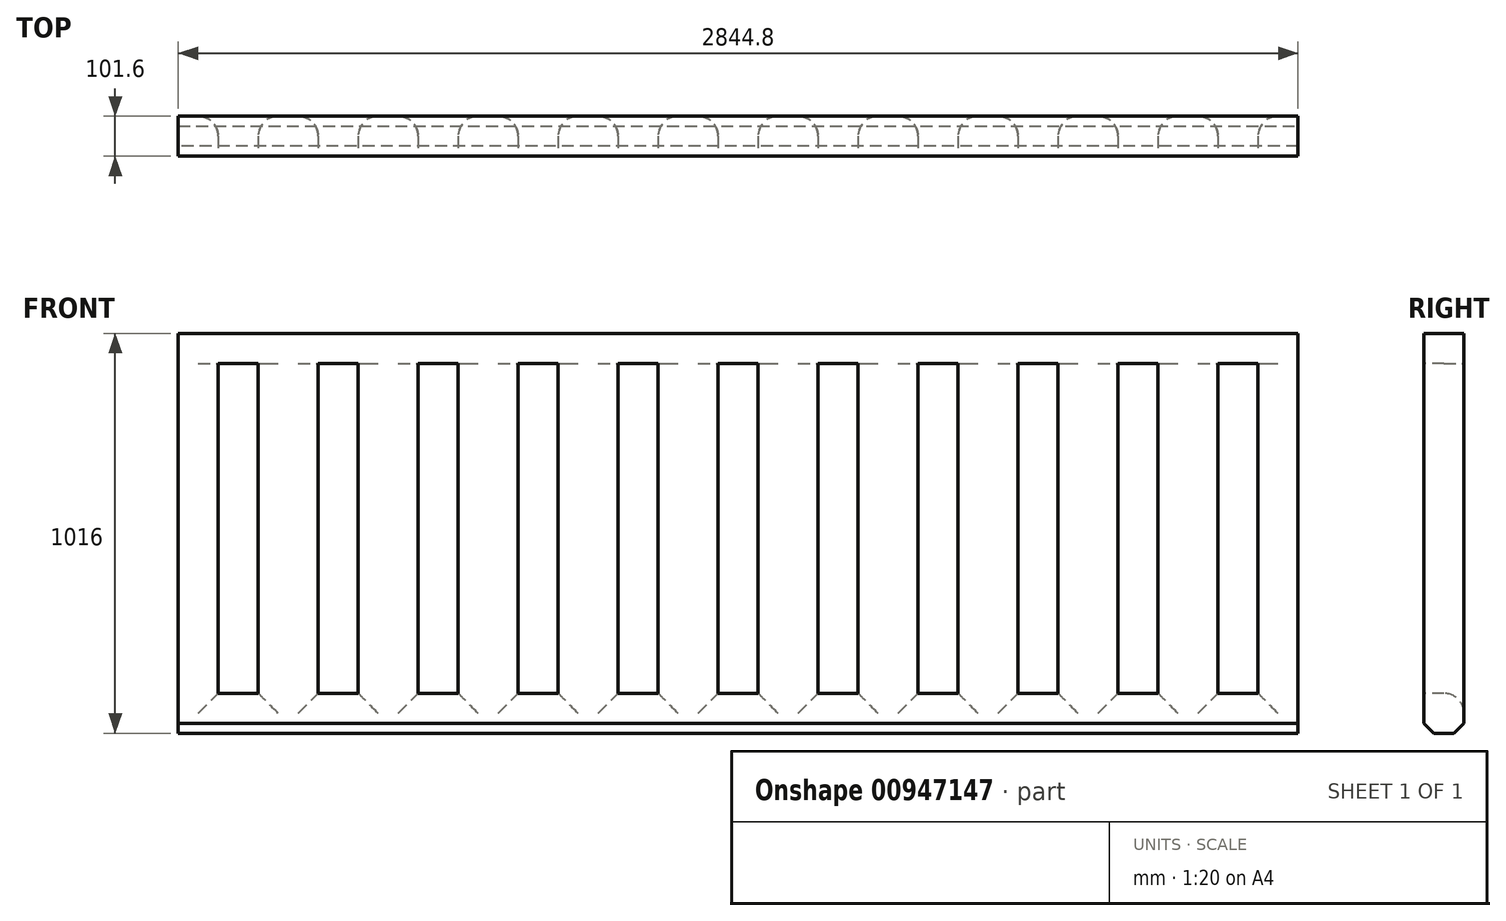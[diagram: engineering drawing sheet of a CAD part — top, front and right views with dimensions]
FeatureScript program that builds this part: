
annotation { "Feature Type Name" : "Feature", "Feature Type Description" : "" }
export const myFeature = defineFeature(function(context is Context, id is Id, definition is map)
    precondition{}
    {
        {
            var Q0;
            Q0=qCreatedBy(makeId("Front.planeOp"),FACE);
            var sketch = newSketch(context, id + "F0", { "sketchPlane" : qUnion([Q0])});
            skLineSegment(sketch, "E0.bottom", {"start": v(0, 0) * mm, "end": v(4368.8, 0) * mm});
            skLineSegment(sketch, "E0.top", {"start": v(0, 1016) * mm, "end": v(4368.8, 1016) * mm});
            skLineSegment(sketch, "E0.left", {"start": v(0, 0) * mm, "end": v(0, 1016) * mm});
            skLineSegment(sketch, "E0.right", {"start": v(4368.8, 0) * mm, "end": v(4368.8, 1016) * mm});
            skLineSegment(sketch, "E1", {"start": v(2844.8, 1016) * mm, "end": v(2844.8, 0) * mm});
            skSolve(sketch);
        }
        {
            var Q0;
            {var subQ0=sQuery(id+"F0.wireOp",EDGE,"E0.left");Q0=makeQuery(id+"F0.imprint","IMPRINT",FACE,{"disambiguationData":[TD([[makeQuery(id+"F0.imprint","IMPRINT",EDGE,{"derivedFrom":subQ0}),-1.0]])]});}
            extrude(context, id + "F1", {"entities" : qUnion([Q0]), "depth" : 101.6 * mm, "offsetDistance" : 25.4 * mm});
        }
        {
            var Q0;
            Q0=makeQuery(id+"F1.opExtrude","CAP_FACE",FACE,{"disambiguationData":[OSD([sQuery(id+"F0.wireOp",EDGE,"E0.bottom"),sQuery(id+"F0.wireOp",EDGE,"E0.top"),sQuery(id+"F0.wireOp",EDGE,"E0.left"),sQuery(id+"F0.wireOp",EDGE,"E0.right")])],"isStart":false});
            var sketch = newSketch(context, id + "F2", { "sketchPlane" : qUnion([Q0])});
            skLineSegment(sketch, "E2.left", {"start": v(101.6, 939.8) * mm, "end": v(101.6, 101.6) * mm});
            skLineSegment(sketch, "E2.right", {"start": v(203.2, 939.8) * mm, "end": v(203.2, 101.6) * mm});
            skLineSegment(sketch, "E3", {"start": v(101.6, 939.8) * mm, "end": v(203.2, 939.8) * mm});
            skLineSegment(sketch, "E4", {"start": v(101.6, 101.6) * mm, "end": v(203.2, 101.6) * mm});
            skLineSegment(sketch, "E5", {"start": v(0, 939.8) * mm, "end": v(2974.6, 939.8) * mm, "construction": true});
            skPoint(sketch, "E5.startSnap0", {"position": v(152.4, 939.8) * mm});
            skLineSegment(sketch, "E6", {"start": v(0, 101.6) * mm, "end": v(2947.62, 101.6) * mm, "construction": true});
            skLineSegment(sketch, "E7.bottom", {"start": v(355.6, 939.8) * mm, "end": v(457.2, 939.8) * mm});
            skLineSegment(sketch, "E7.top", {"start": v(355.6, 101.6) * mm, "end": v(457.2, 101.6) * mm});
            skLineSegment(sketch, "E7.left", {"start": v(355.6, 939.8) * mm, "end": v(355.6, 101.6) * mm});
            skLineSegment(sketch, "E7.right", {"start": v(457.2, 939.8) * mm, "end": v(457.2, 101.6) * mm});
            skLineSegment(sketch, "E8.bottom", {"start": v(609.6, 939.8) * mm, "end": v(711.2, 939.8) * mm});
            skLineSegment(sketch, "E8.top", {"start": v(609.6, 101.6) * mm, "end": v(711.2, 101.6) * mm});
            skLineSegment(sketch, "E8.left", {"start": v(609.6, 939.8) * mm, "end": v(609.6, 101.6) * mm});
            skLineSegment(sketch, "E8.right", {"start": v(711.2, 939.8) * mm, "end": v(711.2, 101.6) * mm});
            skLineSegment(sketch, "E9.bottom", {"start": v(863.6, 939.8) * mm, "end": v(965.2, 939.8) * mm});
            skLineSegment(sketch, "E9.top", {"start": v(863.6, 101.6) * mm, "end": v(965.2, 101.6) * mm});
            skLineSegment(sketch, "E9.left", {"start": v(863.6, 939.8) * mm, "end": v(863.6, 101.6) * mm});
            skLineSegment(sketch, "E9.right", {"start": v(965.2, 939.8) * mm, "end": v(965.2, 101.6) * mm});
            skLineSegment(sketch, "E10.bottom", {"start": v(1117.6, 939.8) * mm, "end": v(1219.2, 939.8) * mm});
            skLineSegment(sketch, "E10.top", {"start": v(1117.6, 101.6) * mm, "end": v(1219.2, 101.6) * mm});
            skLineSegment(sketch, "E10.left", {"start": v(1117.6, 939.8) * mm, "end": v(1117.6, 101.6) * mm});
            skLineSegment(sketch, "E10.right", {"start": v(1219.2, 939.8) * mm, "end": v(1219.2, 101.6) * mm});
            skLineSegment(sketch, "E11.bottom", {"start": v(1371.6, 939.8) * mm, "end": v(1473.2, 939.8) * mm});
            skLineSegment(sketch, "E11.top", {"start": v(1371.6, 101.6) * mm, "end": v(1473.2, 101.6) * mm});
            skLineSegment(sketch, "E11.left", {"start": v(1371.6, 939.8) * mm, "end": v(1371.6, 101.6) * mm});
            skLineSegment(sketch, "E11.right", {"start": v(1473.2, 939.8) * mm, "end": v(1473.2, 101.6) * mm});
            skLineSegment(sketch, "E12.bottom", {"start": v(1625.6, 939.8) * mm, "end": v(1727.2, 939.8) * mm});
            skLineSegment(sketch, "E12.top", {"start": v(1625.6, 101.6) * mm, "end": v(1727.2, 101.6) * mm});
            skLineSegment(sketch, "E12.left", {"start": v(1625.6, 939.8) * mm, "end": v(1625.6, 101.6) * mm});
            skLineSegment(sketch, "E12.right", {"start": v(1727.2, 939.8) * mm, "end": v(1727.2, 101.6) * mm});
            skLineSegment(sketch, "E13.bottom", {"start": v(1879.6, 939.8) * mm, "end": v(1981.2, 939.8) * mm});
            skLineSegment(sketch, "E13.top", {"start": v(1879.6, 101.6) * mm, "end": v(1981.2, 101.6) * mm});
            skLineSegment(sketch, "E13.left", {"start": v(1879.6, 939.8) * mm, "end": v(1879.6, 101.6) * mm});
            skLineSegment(sketch, "E13.right", {"start": v(1981.2, 939.8) * mm, "end": v(1981.2, 101.6) * mm});
            skLineSegment(sketch, "E14.bottom", {"start": v(2133.6, 939.8) * mm, "end": v(2235.2, 939.8) * mm});
            skLineSegment(sketch, "E14.top", {"start": v(2133.6, 101.6) * mm, "end": v(2235.2, 101.6) * mm});
            skLineSegment(sketch, "E14.left", {"start": v(2133.6, 939.8) * mm, "end": v(2133.6, 101.6) * mm});
            skLineSegment(sketch, "E14.right", {"start": v(2235.2, 939.8) * mm, "end": v(2235.2, 101.6) * mm});
            skLineSegment(sketch, "E15.bottom", {"start": v(2387.6, 939.8) * mm, "end": v(2489.2, 939.8) * mm});
            skLineSegment(sketch, "E15.top", {"start": v(2387.6, 101.6) * mm, "end": v(2489.2, 101.6) * mm});
            skLineSegment(sketch, "E15.left", {"start": v(2387.6, 939.8) * mm, "end": v(2387.6, 101.6) * mm});
            skLineSegment(sketch, "E15.right", {"start": v(2489.2, 939.8) * mm, "end": v(2489.2, 101.6) * mm});
            skLineSegment(sketch, "E16.bottom", {"start": v(2641.6, 939.8) * mm, "end": v(2743.2, 939.8) * mm});
            skLineSegment(sketch, "E16.top", {"start": v(2641.6, 101.6) * mm, "end": v(2743.2, 101.6) * mm});
            skLineSegment(sketch, "E16.left", {"start": v(2641.6, 939.8) * mm, "end": v(2641.6, 101.6) * mm});
            skLineSegment(sketch, "E16.right", {"start": v(2743.2, 939.8) * mm, "end": v(2743.2, 101.6) * mm});
            skLineSegment(sketch, "E17.bottom", {"start": v(2941.58, 939.8) * mm, "end": v(3043.18, 939.8) * mm});
            skLineSegment(sketch, "E17.top", {"start": v(2941.58, 101.6) * mm, "end": v(3043.18, 101.6) * mm});
            skLineSegment(sketch, "E17.left", {"start": v(2941.58, 939.8) * mm, "end": v(2941.58, 101.6) * mm});
            skLineSegment(sketch, "E17.right", {"start": v(3043.18, 939.8) * mm, "end": v(3043.18, 101.6) * mm});
            skSolve(sketch);
        }
        {
            var Q0;
            {var subQ0=sQuery(id+"F2.wireOp",EDGE,"E3");Q0=makeQuery(id+"F2.imprint","IMPRINT",FACE,{"disambiguationData":[TD([[makeQuery(id+"F2.imprint","IMPRINT",EDGE,{"derivedFrom":subQ0}),-1.0]])]});}
            var Q1;
            Q1=makeQuery(id+"F2.imprint","IMPRINT",FACE,{"disambiguationData":[TD([[makeQuery(id+"F2.imprint","IMPRINT",EDGE,{"derivedFrom":sQuery(id+"F2.wireOp",EDGE,"E7.bottom")}),-1.0]])]});
            var Q2;
            Q2=makeQuery(id+"F2.imprint","IMPRINT",FACE,{"disambiguationData":[TD([[makeQuery(id+"F2.imprint","IMPRINT",EDGE,{"derivedFrom":sQuery(id+"F2.wireOp",EDGE,"E8.bottom")}),-1.0]])]});
            var Q3;
            Q3=makeQuery(id+"F2.imprint","IMPRINT",FACE,{"disambiguationData":[TD([[makeQuery(id+"F2.imprint","IMPRINT",EDGE,{"derivedFrom":sQuery(id+"F2.wireOp",EDGE,"E9.bottom")}),-1.0]])]});
            var Q4;
            Q4=makeQuery(id+"F2.imprint","IMPRINT",FACE,{"disambiguationData":[TD([[makeQuery(id+"F2.imprint","IMPRINT",EDGE,{"derivedFrom":sQuery(id+"F2.wireOp",EDGE,"E10.bottom")}),-1.0]])]});
            var Q5;
            Q5=makeQuery(id+"F2.imprint","IMPRINT",FACE,{"disambiguationData":[TD([[makeQuery(id+"F2.imprint","IMPRINT",EDGE,{"derivedFrom":sQuery(id+"F2.wireOp",EDGE,"E11.bottom")}),-1.0]])]});
            var Q6;
            Q6=makeQuery(id+"F2.imprint","IMPRINT",FACE,{"disambiguationData":[TD([[makeQuery(id+"F2.imprint","IMPRINT",EDGE,{"derivedFrom":sQuery(id+"F2.wireOp",EDGE,"E12.bottom")}),-1.0]])]});
            var Q7;
            Q7=makeQuery(id+"F2.imprint","IMPRINT",FACE,{"disambiguationData":[TD([[makeQuery(id+"F2.imprint","IMPRINT",EDGE,{"derivedFrom":sQuery(id+"F2.wireOp",EDGE,"E13.bottom")}),-1.0]])]});
            var Q8;
            Q8=makeQuery(id+"F2.imprint","IMPRINT",FACE,{"disambiguationData":[TD([[makeQuery(id+"F2.imprint","IMPRINT",EDGE,{"derivedFrom":sQuery(id+"F2.wireOp",EDGE,"E14.bottom")}),-1.0]])]});
            var Q9;
            Q9=makeQuery(id+"F2.imprint","IMPRINT",FACE,{"disambiguationData":[TD([[makeQuery(id+"F2.imprint","IMPRINT",EDGE,{"derivedFrom":sQuery(id+"F2.wireOp",EDGE,"E15.bottom")}),-1.0]])]});
            var Q10;
            Q10=makeQuery(id+"F2.imprint","IMPRINT",FACE,{"disambiguationData":[TD([[makeQuery(id+"F2.imprint","IMPRINT",EDGE,{"derivedFrom":sQuery(id+"F2.wireOp",EDGE,"E16.bottom")}),-1.0]])]});
            extrude(context, id + "F3", {"entities" : qUnion([Q0, Q1, Q2, Q3, Q4, Q5, Q6, Q7, Q8, Q9, Q10]), "operationType" : NewBodyOperationType.REMOVE, "oppositeDirection" : true, "depth" : 307.34 * mm, "offsetDistance" : 25.4 * mm});
        }
        {
            var Q0;
            Q0=makeQuery(id+"F3.boolean.opBoolean","COPY",EDGE,{"derivedFrom":makeQuery(id+"F3.opExtrude","CAP_EDGE",EDGE,{"disambiguationData":[OSD([sQuery(id+"F2.wireOp",EDGE,"E2.left")])],"isStart":true})});
            var Q1;
            Q1=makeQuery(id+"F3.boolean.opBoolean","COPY",EDGE,{"derivedFrom":makeQuery(id+"F3.opExtrude","CAP_EDGE",EDGE,{"disambiguationData":[OSD([sQuery(id+"F2.wireOp",EDGE,"E3")])],"isStart":true})});
            var Q2;
            Q2=makeQuery(id+"F3.boolean.opBoolean","COPY",EDGE,{"derivedFrom":makeQuery(id+"F3.opExtrude","CAP_EDGE",EDGE,{"disambiguationData":[OSD([sQuery(id+"F2.wireOp",EDGE,"E2.right")])],"isStart":true})});
            var Q3;
            Q3=makeQuery(id+"F3.boolean.opBoolean","COPY",EDGE,{"derivedFrom":makeQuery(id+"F3.opExtrude","CAP_EDGE",EDGE,{"disambiguationData":[OSD([sQuery(id+"F2.wireOp",EDGE,"E4")])],"isStart":true})});
            var Q4;
            Q4=makeQuery(id+"F3.boolean.opBoolean","COPY",EDGE,{"derivedFrom":makeQuery(id+"F3.opExtrude","CAP_EDGE",EDGE,{"disambiguationData":[OSD([sQuery(id+"F2.wireOp",EDGE,"E7.left")])],"isStart":true})});
            var Q5;
            Q5=makeQuery(id+"F3.boolean.opBoolean","COPY",EDGE,{"derivedFrom":makeQuery(id+"F3.opExtrude","CAP_EDGE",EDGE,{"disambiguationData":[OSD([sQuery(id+"F2.wireOp",EDGE,"E7.bottom")])],"isStart":true})});
            var Q6;
            Q6=makeQuery(id+"F3.boolean.opBoolean","COPY",EDGE,{"derivedFrom":makeQuery(id+"F3.opExtrude","CAP_EDGE",EDGE,{"disambiguationData":[OSD([sQuery(id+"F2.wireOp",EDGE,"E7.right")])],"isStart":true})});
            var Q7;
            Q7=makeQuery(id+"F3.boolean.opBoolean","COPY",EDGE,{"derivedFrom":makeQuery(id+"F3.opExtrude","CAP_EDGE",EDGE,{"disambiguationData":[OSD([sQuery(id+"F2.wireOp",EDGE,"E7.top")])],"isStart":true})});
            var Q8;
            Q8=makeQuery(id+"F3.boolean.opBoolean","COPY",EDGE,{"derivedFrom":makeQuery(id+"F3.opExtrude","CAP_EDGE",EDGE,{"disambiguationData":[OSD([sQuery(id+"F2.wireOp",EDGE,"E8.left")])],"isStart":true})});
            var Q9;
            Q9=makeQuery(id+"F3.boolean.opBoolean","COPY",EDGE,{"derivedFrom":makeQuery(id+"F3.opExtrude","CAP_EDGE",EDGE,{"disambiguationData":[OSD([sQuery(id+"F2.wireOp",EDGE,"E8.top")])],"isStart":true})});
            var Q10;
            Q10=makeQuery(id+"F3.boolean.opBoolean","COPY",EDGE,{"derivedFrom":makeQuery(id+"F3.opExtrude","CAP_EDGE",EDGE,{"disambiguationData":[OSD([sQuery(id+"F2.wireOp",EDGE,"E8.right")])],"isStart":true})});
            var Q11;
            Q11=makeQuery(id+"F3.boolean.opBoolean","COPY",EDGE,{"derivedFrom":makeQuery(id+"F3.opExtrude","CAP_EDGE",EDGE,{"disambiguationData":[OSD([sQuery(id+"F2.wireOp",EDGE,"E8.bottom")])],"isStart":true})});
            var Q12;
            Q12=makeQuery(id+"F3.boolean.opBoolean","COPY",EDGE,{"derivedFrom":makeQuery(id+"F3.opExtrude","CAP_EDGE",EDGE,{"disambiguationData":[OSD([sQuery(id+"F2.wireOp",EDGE,"E9.left")])],"isStart":true})});
            var Q13;
            Q13=makeQuery(id+"F3.boolean.opBoolean","COPY",EDGE,{"derivedFrom":makeQuery(id+"F3.opExtrude","CAP_EDGE",EDGE,{"disambiguationData":[OSD([sQuery(id+"F2.wireOp",EDGE,"E9.bottom")])],"isStart":true})});
            var Q14;
            Q14=makeQuery(id+"F3.boolean.opBoolean","COPY",EDGE,{"derivedFrom":makeQuery(id+"F3.opExtrude","CAP_EDGE",EDGE,{"disambiguationData":[OSD([sQuery(id+"F2.wireOp",EDGE,"E9.right")])],"isStart":true})});
            var Q15;
            Q15=makeQuery(id+"F3.boolean.opBoolean","COPY",EDGE,{"derivedFrom":makeQuery(id+"F3.opExtrude","CAP_EDGE",EDGE,{"disambiguationData":[OSD([sQuery(id+"F2.wireOp",EDGE,"E9.top")])],"isStart":true})});
            var Q16;
            Q16=makeQuery(id+"F3.boolean.opBoolean","COPY",EDGE,{"derivedFrom":makeQuery(id+"F3.opExtrude","CAP_EDGE",EDGE,{"disambiguationData":[OSD([sQuery(id+"F2.wireOp",EDGE,"E10.left")])],"isStart":true})});
            var Q17;
            Q17=makeQuery(id+"F3.boolean.opBoolean","COPY",EDGE,{"derivedFrom":makeQuery(id+"F3.opExtrude","CAP_EDGE",EDGE,{"disambiguationData":[OSD([sQuery(id+"F2.wireOp",EDGE,"E10.top")])],"isStart":true})});
            var Q18;
            Q18=makeQuery(id+"F3.boolean.opBoolean","COPY",EDGE,{"derivedFrom":makeQuery(id+"F3.opExtrude","CAP_EDGE",EDGE,{"disambiguationData":[OSD([sQuery(id+"F2.wireOp",EDGE,"E10.right")])],"isStart":true})});
            var Q19;
            Q19=makeQuery(id+"F3.boolean.opBoolean","COPY",EDGE,{"derivedFrom":makeQuery(id+"F3.opExtrude","CAP_EDGE",EDGE,{"disambiguationData":[OSD([sQuery(id+"F2.wireOp",EDGE,"E10.bottom")])],"isStart":true})});
            var Q20;
            Q20=makeQuery(id+"F3.boolean.opBoolean","COPY",EDGE,{"derivedFrom":makeQuery(id+"F3.opExtrude","CAP_EDGE",EDGE,{"disambiguationData":[OSD([sQuery(id+"F2.wireOp",EDGE,"E11.bottom")])],"isStart":true})});
            var Q21;
            Q21=makeQuery(id+"F3.boolean.opBoolean","COPY",EDGE,{"derivedFrom":makeQuery(id+"F3.opExtrude","CAP_EDGE",EDGE,{"disambiguationData":[OSD([sQuery(id+"F2.wireOp",EDGE,"E11.left")])],"isStart":true})});
            var Q22;
            Q22=makeQuery(id+"F3.boolean.opBoolean","COPY",EDGE,{"derivedFrom":makeQuery(id+"F3.opExtrude","CAP_EDGE",EDGE,{"disambiguationData":[OSD([sQuery(id+"F2.wireOp",EDGE,"E11.right")])],"isStart":true})});
            var Q23;
            Q23=makeQuery(id+"F3.boolean.opBoolean","COPY",EDGE,{"derivedFrom":makeQuery(id+"F3.opExtrude","CAP_EDGE",EDGE,{"disambiguationData":[OSD([sQuery(id+"F2.wireOp",EDGE,"E11.top")])],"isStart":true})});
            var Q24;
            Q24=makeQuery(id+"F3.boolean.opBoolean","COPY",EDGE,{"derivedFrom":makeQuery(id+"F3.opExtrude","CAP_EDGE",EDGE,{"disambiguationData":[OSD([sQuery(id+"F2.wireOp",EDGE,"E12.top")])],"isStart":true})});
            var Q25;
            Q25=makeQuery(id+"F3.boolean.opBoolean","COPY",EDGE,{"derivedFrom":makeQuery(id+"F3.opExtrude","CAP_EDGE",EDGE,{"disambiguationData":[OSD([sQuery(id+"F2.wireOp",EDGE,"E12.left")])],"isStart":true})});
            var Q26;
            Q26=makeQuery(id+"F3.boolean.opBoolean","COPY",EDGE,{"derivedFrom":makeQuery(id+"F3.opExtrude","CAP_EDGE",EDGE,{"disambiguationData":[OSD([sQuery(id+"F2.wireOp",EDGE,"E12.right")])],"isStart":true})});
            var Q27;
            Q27=makeQuery(id+"F3.boolean.opBoolean","COPY",EDGE,{"derivedFrom":makeQuery(id+"F3.opExtrude","CAP_EDGE",EDGE,{"disambiguationData":[OSD([sQuery(id+"F2.wireOp",EDGE,"E12.bottom")])],"isStart":true})});
            var Q28;
            Q28=makeQuery(id+"F3.boolean.opBoolean","COPY",EDGE,{"derivedFrom":makeQuery(id+"F3.opExtrude","CAP_EDGE",EDGE,{"disambiguationData":[OSD([sQuery(id+"F2.wireOp",EDGE,"E13.left")])],"isStart":true})});
            var Q29;
            Q29=makeQuery(id+"F3.boolean.opBoolean","COPY",EDGE,{"derivedFrom":makeQuery(id+"F3.opExtrude","CAP_EDGE",EDGE,{"disambiguationData":[OSD([sQuery(id+"F2.wireOp",EDGE,"E13.bottom")])],"isStart":true})});
            var Q30;
            Q30=makeQuery(id+"F3.boolean.opBoolean","COPY",EDGE,{"derivedFrom":makeQuery(id+"F3.opExtrude","CAP_EDGE",EDGE,{"disambiguationData":[OSD([sQuery(id+"F2.wireOp",EDGE,"E13.right")])],"isStart":true})});
            var Q31;
            Q31=makeQuery(id+"F3.boolean.opBoolean","COPY",EDGE,{"derivedFrom":makeQuery(id+"F3.opExtrude","CAP_EDGE",EDGE,{"disambiguationData":[OSD([sQuery(id+"F2.wireOp",EDGE,"E13.top")])],"isStart":true})});
            var Q32;
            Q32=makeQuery(id+"F3.boolean.opBoolean","COPY",EDGE,{"derivedFrom":makeQuery(id+"F3.opExtrude","CAP_EDGE",EDGE,{"disambiguationData":[OSD([sQuery(id+"F2.wireOp",EDGE,"E14.top")])],"isStart":true})});
            var Q33;
            Q33=makeQuery(id+"F3.boolean.opBoolean","COPY",EDGE,{"derivedFrom":makeQuery(id+"F3.opExtrude","CAP_EDGE",EDGE,{"disambiguationData":[OSD([sQuery(id+"F2.wireOp",EDGE,"E14.left")])],"isStart":true})});
            var Q34;
            Q34=makeQuery(id+"F3.boolean.opBoolean","COPY",EDGE,{"derivedFrom":makeQuery(id+"F3.opExtrude","CAP_EDGE",EDGE,{"disambiguationData":[OSD([sQuery(id+"F2.wireOp",EDGE,"E14.right")])],"isStart":true})});
            var Q35;
            Q35=makeQuery(id+"F3.boolean.opBoolean","COPY",EDGE,{"derivedFrom":makeQuery(id+"F3.opExtrude","CAP_EDGE",EDGE,{"disambiguationData":[OSD([sQuery(id+"F2.wireOp",EDGE,"E14.bottom")])],"isStart":true})});
            var Q36;
            Q36=makeQuery(id+"F3.boolean.opBoolean","COPY",EDGE,{"derivedFrom":makeQuery(id+"F3.opExtrude","CAP_EDGE",EDGE,{"disambiguationData":[OSD([sQuery(id+"F2.wireOp",EDGE,"E15.bottom")])],"isStart":true})});
            var Q37;
            Q37=makeQuery(id+"F3.boolean.opBoolean","COPY",EDGE,{"derivedFrom":makeQuery(id+"F3.opExtrude","CAP_EDGE",EDGE,{"disambiguationData":[OSD([sQuery(id+"F2.wireOp",EDGE,"E15.left")])],"isStart":true})});
            var Q38;
            Q38=makeQuery(id+"F3.boolean.opBoolean","COPY",EDGE,{"derivedFrom":makeQuery(id+"F3.opExtrude","CAP_EDGE",EDGE,{"disambiguationData":[OSD([sQuery(id+"F2.wireOp",EDGE,"E15.right")])],"isStart":true})});
            var Q39;
            Q39=makeQuery(id+"F3.boolean.opBoolean","COPY",EDGE,{"derivedFrom":makeQuery(id+"F3.opExtrude","CAP_EDGE",EDGE,{"disambiguationData":[OSD([sQuery(id+"F2.wireOp",EDGE,"E15.top")])],"isStart":true})});
            var Q40;
            Q40=makeQuery(id+"F3.boolean.opBoolean","COPY",EDGE,{"derivedFrom":makeQuery(id+"F3.opExtrude","CAP_EDGE",EDGE,{"disambiguationData":[OSD([sQuery(id+"F2.wireOp",EDGE,"E16.left")])],"isStart":true})});
            var Q41;
            Q41=makeQuery(id+"F3.boolean.opBoolean","COPY",EDGE,{"derivedFrom":makeQuery(id+"F3.opExtrude","CAP_EDGE",EDGE,{"disambiguationData":[OSD([sQuery(id+"F2.wireOp",EDGE,"E16.top")])],"isStart":true})});
            var Q42;
            Q42=makeQuery(id+"F3.boolean.opBoolean","COPY",EDGE,{"derivedFrom":makeQuery(id+"F3.opExtrude","CAP_EDGE",EDGE,{"disambiguationData":[OSD([sQuery(id+"F2.wireOp",EDGE,"E16.right")])],"isStart":true})});
            var Q43;
            Q43=makeQuery(id+"F3.boolean.opBoolean","INTERSECT",EDGE,{"derivedFrom":[makeQuery(id+"F1.opExtrude","CAP_FACE",FACE,{"disambiguationData":[OSD([sQuery(id+"F0.wireOp",EDGE,"E0.bottom"),sQuery(id+"F0.wireOp",EDGE,"E0.top"),sQuery(id+"F0.wireOp",EDGE,"E0.left"),sQuery(id+"F0.wireOp",EDGE,"E1")])],"isStart":true}),makeQuery(id+"F3.opExtrude","SWEPT_FACE",FACE,{"disambiguationData":[OSD([sQuery(id+"F2.wireOp",EDGE,"E4")])]})]});
            var Q44;
            Q44=makeQuery(id+"F3.boolean.opBoolean","INTERSECT",EDGE,{"derivedFrom":[makeQuery(id+"F1.opExtrude","CAP_FACE",FACE,{"disambiguationData":[OSD([sQuery(id+"F0.wireOp",EDGE,"E0.bottom"),sQuery(id+"F0.wireOp",EDGE,"E0.top"),sQuery(id+"F0.wireOp",EDGE,"E0.left"),sQuery(id+"F0.wireOp",EDGE,"E1")])],"isStart":true}),makeQuery(id+"F3.opExtrude","SWEPT_FACE",FACE,{"disambiguationData":[OSD([sQuery(id+"F2.wireOp",EDGE,"E2.left")])]})]});
            var Q45;
            Q45=makeQuery(id+"F3.boolean.opBoolean","INTERSECT",EDGE,{"derivedFrom":[makeQuery(id+"F1.opExtrude","CAP_FACE",FACE,{"disambiguationData":[OSD([sQuery(id+"F0.wireOp",EDGE,"E0.bottom"),sQuery(id+"F0.wireOp",EDGE,"E0.top"),sQuery(id+"F0.wireOp",EDGE,"E0.left"),sQuery(id+"F0.wireOp",EDGE,"E1")])],"isStart":true}),makeQuery(id+"F3.opExtrude","SWEPT_FACE",FACE,{"disambiguationData":[OSD([sQuery(id+"F2.wireOp",EDGE,"E2.right")])]})]});
            var Q46;
            Q46=makeQuery(id+"F3.boolean.opBoolean","INTERSECT",EDGE,{"derivedFrom":[makeQuery(id+"F1.opExtrude","CAP_FACE",FACE,{"disambiguationData":[OSD([sQuery(id+"F0.wireOp",EDGE,"E0.bottom"),sQuery(id+"F0.wireOp",EDGE,"E0.top"),sQuery(id+"F0.wireOp",EDGE,"E0.left"),sQuery(id+"F0.wireOp",EDGE,"E1")])],"isStart":true}),makeQuery(id+"F3.opExtrude","SWEPT_FACE",FACE,{"disambiguationData":[OSD([sQuery(id+"F2.wireOp",EDGE,"E7.left")])]})]});
            var Q47;
            Q47=makeQuery(id+"F3.boolean.opBoolean","INTERSECT",EDGE,{"derivedFrom":[makeQuery(id+"F1.opExtrude","CAP_FACE",FACE,{"disambiguationData":[OSD([sQuery(id+"F0.wireOp",EDGE,"E0.bottom"),sQuery(id+"F0.wireOp",EDGE,"E0.top"),sQuery(id+"F0.wireOp",EDGE,"E0.left"),sQuery(id+"F0.wireOp",EDGE,"E1")])],"isStart":true}),makeQuery(id+"F3.opExtrude","SWEPT_FACE",FACE,{"disambiguationData":[OSD([sQuery(id+"F2.wireOp",EDGE,"E7.top")])]})]});
            var Q48;
            Q48=makeQuery(id+"F3.boolean.opBoolean","INTERSECT",EDGE,{"derivedFrom":[makeQuery(id+"F1.opExtrude","CAP_FACE",FACE,{"disambiguationData":[OSD([sQuery(id+"F0.wireOp",EDGE,"E0.bottom"),sQuery(id+"F0.wireOp",EDGE,"E0.top"),sQuery(id+"F0.wireOp",EDGE,"E0.left"),sQuery(id+"F0.wireOp",EDGE,"E1")])],"isStart":true}),makeQuery(id+"F3.opExtrude","SWEPT_FACE",FACE,{"disambiguationData":[OSD([sQuery(id+"F2.wireOp",EDGE,"E7.right")])]})]});
            var Q49;
            Q49=makeQuery(id+"F3.boolean.opBoolean","INTERSECT",EDGE,{"derivedFrom":[makeQuery(id+"F1.opExtrude","CAP_FACE",FACE,{"disambiguationData":[OSD([sQuery(id+"F0.wireOp",EDGE,"E0.bottom"),sQuery(id+"F0.wireOp",EDGE,"E0.top"),sQuery(id+"F0.wireOp",EDGE,"E0.left"),sQuery(id+"F0.wireOp",EDGE,"E1")])],"isStart":true}),makeQuery(id+"F3.opExtrude","SWEPT_FACE",FACE,{"disambiguationData":[OSD([sQuery(id+"F2.wireOp",EDGE,"E8.left")])]})]});
            var Q50;
            Q50=makeQuery(id+"F3.boolean.opBoolean","INTERSECT",EDGE,{"derivedFrom":[makeQuery(id+"F1.opExtrude","CAP_FACE",FACE,{"disambiguationData":[OSD([sQuery(id+"F0.wireOp",EDGE,"E0.bottom"),sQuery(id+"F0.wireOp",EDGE,"E0.top"),sQuery(id+"F0.wireOp",EDGE,"E0.left"),sQuery(id+"F0.wireOp",EDGE,"E1")])],"isStart":true}),makeQuery(id+"F3.opExtrude","SWEPT_FACE",FACE,{"disambiguationData":[OSD([sQuery(id+"F2.wireOp",EDGE,"E8.top")])]})]});
            var Q51;
            Q51=makeQuery(id+"F3.boolean.opBoolean","INTERSECT",EDGE,{"derivedFrom":[makeQuery(id+"F1.opExtrude","CAP_FACE",FACE,{"disambiguationData":[OSD([sQuery(id+"F0.wireOp",EDGE,"E0.bottom"),sQuery(id+"F0.wireOp",EDGE,"E0.top"),sQuery(id+"F0.wireOp",EDGE,"E0.left"),sQuery(id+"F0.wireOp",EDGE,"E1")])],"isStart":true}),makeQuery(id+"F3.opExtrude","SWEPT_FACE",FACE,{"disambiguationData":[OSD([sQuery(id+"F2.wireOp",EDGE,"E8.right")])]})]});
            var Q52;
            Q52=makeQuery(id+"F3.boolean.opBoolean","INTERSECT",EDGE,{"derivedFrom":[makeQuery(id+"F1.opExtrude","CAP_FACE",FACE,{"disambiguationData":[OSD([sQuery(id+"F0.wireOp",EDGE,"E0.bottom"),sQuery(id+"F0.wireOp",EDGE,"E0.top"),sQuery(id+"F0.wireOp",EDGE,"E0.left"),sQuery(id+"F0.wireOp",EDGE,"E1")])],"isStart":true}),makeQuery(id+"F3.opExtrude","SWEPT_FACE",FACE,{"disambiguationData":[OSD([sQuery(id+"F2.wireOp",EDGE,"E9.left")])]})]});
            var Q53;
            Q53=makeQuery(id+"F3.boolean.opBoolean","INTERSECT",EDGE,{"derivedFrom":[makeQuery(id+"F1.opExtrude","CAP_FACE",FACE,{"disambiguationData":[OSD([sQuery(id+"F0.wireOp",EDGE,"E0.bottom"),sQuery(id+"F0.wireOp",EDGE,"E0.top"),sQuery(id+"F0.wireOp",EDGE,"E0.left"),sQuery(id+"F0.wireOp",EDGE,"E1")])],"isStart":true}),makeQuery(id+"F3.opExtrude","SWEPT_FACE",FACE,{"disambiguationData":[OSD([sQuery(id+"F2.wireOp",EDGE,"E9.top")])]})]});
            var Q54;
            Q54=makeQuery(id+"F3.boolean.opBoolean","INTERSECT",EDGE,{"derivedFrom":[makeQuery(id+"F1.opExtrude","CAP_FACE",FACE,{"disambiguationData":[OSD([sQuery(id+"F0.wireOp",EDGE,"E0.bottom"),sQuery(id+"F0.wireOp",EDGE,"E0.top"),sQuery(id+"F0.wireOp",EDGE,"E0.left"),sQuery(id+"F0.wireOp",EDGE,"E1")])],"isStart":true}),makeQuery(id+"F3.opExtrude","SWEPT_FACE",FACE,{"disambiguationData":[OSD([sQuery(id+"F2.wireOp",EDGE,"E9.right")])]})]});
            var Q55;
            Q55=makeQuery(id+"F3.boolean.opBoolean","INTERSECT",EDGE,{"derivedFrom":[makeQuery(id+"F1.opExtrude","CAP_FACE",FACE,{"disambiguationData":[OSD([sQuery(id+"F0.wireOp",EDGE,"E0.bottom"),sQuery(id+"F0.wireOp",EDGE,"E0.top"),sQuery(id+"F0.wireOp",EDGE,"E0.left"),sQuery(id+"F0.wireOp",EDGE,"E1")])],"isStart":true}),makeQuery(id+"F3.opExtrude","SWEPT_FACE",FACE,{"disambiguationData":[OSD([sQuery(id+"F2.wireOp",EDGE,"E10.left")])]})]});
            var Q56;
            Q56=makeQuery(id+"F3.boolean.opBoolean","INTERSECT",EDGE,{"derivedFrom":[makeQuery(id+"F1.opExtrude","CAP_FACE",FACE,{"disambiguationData":[OSD([sQuery(id+"F0.wireOp",EDGE,"E0.bottom"),sQuery(id+"F0.wireOp",EDGE,"E0.top"),sQuery(id+"F0.wireOp",EDGE,"E0.left"),sQuery(id+"F0.wireOp",EDGE,"E1")])],"isStart":true}),makeQuery(id+"F3.opExtrude","SWEPT_FACE",FACE,{"disambiguationData":[OSD([sQuery(id+"F2.wireOp",EDGE,"E10.top")])]})]});
            var Q57;
            Q57=makeQuery(id+"F3.boolean.opBoolean","INTERSECT",EDGE,{"derivedFrom":[makeQuery(id+"F1.opExtrude","CAP_FACE",FACE,{"disambiguationData":[OSD([sQuery(id+"F0.wireOp",EDGE,"E0.bottom"),sQuery(id+"F0.wireOp",EDGE,"E0.top"),sQuery(id+"F0.wireOp",EDGE,"E0.left"),sQuery(id+"F0.wireOp",EDGE,"E1")])],"isStart":true}),makeQuery(id+"F3.opExtrude","SWEPT_FACE",FACE,{"disambiguationData":[OSD([sQuery(id+"F2.wireOp",EDGE,"E10.right")])]})]});
            var Q58;
            Q58=makeQuery(id+"F3.boolean.opBoolean","INTERSECT",EDGE,{"derivedFrom":[makeQuery(id+"F1.opExtrude","CAP_FACE",FACE,{"disambiguationData":[OSD([sQuery(id+"F0.wireOp",EDGE,"E0.bottom"),sQuery(id+"F0.wireOp",EDGE,"E0.top"),sQuery(id+"F0.wireOp",EDGE,"E0.left"),sQuery(id+"F0.wireOp",EDGE,"E1")])],"isStart":true}),makeQuery(id+"F3.opExtrude","SWEPT_FACE",FACE,{"disambiguationData":[OSD([sQuery(id+"F2.wireOp",EDGE,"E11.top")])]})]});
            var Q59;
            Q59=makeQuery(id+"F3.boolean.opBoolean","INTERSECT",EDGE,{"derivedFrom":[makeQuery(id+"F1.opExtrude","CAP_FACE",FACE,{"disambiguationData":[OSD([sQuery(id+"F0.wireOp",EDGE,"E0.bottom"),sQuery(id+"F0.wireOp",EDGE,"E0.top"),sQuery(id+"F0.wireOp",EDGE,"E0.left"),sQuery(id+"F0.wireOp",EDGE,"E1")])],"isStart":true}),makeQuery(id+"F3.opExtrude","SWEPT_FACE",FACE,{"disambiguationData":[OSD([sQuery(id+"F2.wireOp",EDGE,"E11.right")])]})]});
            var Q60;
            Q60=makeQuery(id+"F3.boolean.opBoolean","INTERSECT",EDGE,{"derivedFrom":[makeQuery(id+"F1.opExtrude","CAP_FACE",FACE,{"disambiguationData":[OSD([sQuery(id+"F0.wireOp",EDGE,"E0.bottom"),sQuery(id+"F0.wireOp",EDGE,"E0.top"),sQuery(id+"F0.wireOp",EDGE,"E0.left"),sQuery(id+"F0.wireOp",EDGE,"E1")])],"isStart":true}),makeQuery(id+"F3.opExtrude","SWEPT_FACE",FACE,{"disambiguationData":[OSD([sQuery(id+"F2.wireOp",EDGE,"E11.left")])]})]});
            var Q61;
            Q61=makeQuery(id+"F3.boolean.opBoolean","INTERSECT",EDGE,{"derivedFrom":[makeQuery(id+"F1.opExtrude","CAP_FACE",FACE,{"disambiguationData":[OSD([sQuery(id+"F0.wireOp",EDGE,"E0.bottom"),sQuery(id+"F0.wireOp",EDGE,"E0.top"),sQuery(id+"F0.wireOp",EDGE,"E0.left"),sQuery(id+"F0.wireOp",EDGE,"E1")])],"isStart":true}),makeQuery(id+"F3.opExtrude","SWEPT_FACE",FACE,{"disambiguationData":[OSD([sQuery(id+"F2.wireOp",EDGE,"E12.left")])]})]});
            var Q62;
            Q62=makeQuery(id+"F3.boolean.opBoolean","INTERSECT",EDGE,{"derivedFrom":[makeQuery(id+"F1.opExtrude","CAP_FACE",FACE,{"disambiguationData":[OSD([sQuery(id+"F0.wireOp",EDGE,"E0.bottom"),sQuery(id+"F0.wireOp",EDGE,"E0.top"),sQuery(id+"F0.wireOp",EDGE,"E0.left"),sQuery(id+"F0.wireOp",EDGE,"E1")])],"isStart":true}),makeQuery(id+"F3.opExtrude","SWEPT_FACE",FACE,{"disambiguationData":[OSD([sQuery(id+"F2.wireOp",EDGE,"E12.top")])]})]});
            var Q63;
            Q63=makeQuery(id+"F3.boolean.opBoolean","INTERSECT",EDGE,{"derivedFrom":[makeQuery(id+"F1.opExtrude","CAP_FACE",FACE,{"disambiguationData":[OSD([sQuery(id+"F0.wireOp",EDGE,"E0.bottom"),sQuery(id+"F0.wireOp",EDGE,"E0.top"),sQuery(id+"F0.wireOp",EDGE,"E0.left"),sQuery(id+"F0.wireOp",EDGE,"E1")])],"isStart":true}),makeQuery(id+"F3.opExtrude","SWEPT_FACE",FACE,{"disambiguationData":[OSD([sQuery(id+"F2.wireOp",EDGE,"E12.right")])]})]});
            var Q64;
            Q64=makeQuery(id+"F3.boolean.opBoolean","INTERSECT",EDGE,{"derivedFrom":[makeQuery(id+"F1.opExtrude","CAP_FACE",FACE,{"disambiguationData":[OSD([sQuery(id+"F0.wireOp",EDGE,"E0.bottom"),sQuery(id+"F0.wireOp",EDGE,"E0.top"),sQuery(id+"F0.wireOp",EDGE,"E0.left"),sQuery(id+"F0.wireOp",EDGE,"E1")])],"isStart":true}),makeQuery(id+"F3.opExtrude","SWEPT_FACE",FACE,{"disambiguationData":[OSD([sQuery(id+"F2.wireOp",EDGE,"E13.left")])]})]});
            var Q65;
            Q65=makeQuery(id+"F3.boolean.opBoolean","INTERSECT",EDGE,{"derivedFrom":[makeQuery(id+"F1.opExtrude","CAP_FACE",FACE,{"disambiguationData":[OSD([sQuery(id+"F0.wireOp",EDGE,"E0.bottom"),sQuery(id+"F0.wireOp",EDGE,"E0.top"),sQuery(id+"F0.wireOp",EDGE,"E0.left"),sQuery(id+"F0.wireOp",EDGE,"E1")])],"isStart":true}),makeQuery(id+"F3.opExtrude","SWEPT_FACE",FACE,{"disambiguationData":[OSD([sQuery(id+"F2.wireOp",EDGE,"E13.top")])]})]});
            var Q66;
            Q66=makeQuery(id+"F3.boolean.opBoolean","INTERSECT",EDGE,{"derivedFrom":[makeQuery(id+"F1.opExtrude","CAP_FACE",FACE,{"disambiguationData":[OSD([sQuery(id+"F0.wireOp",EDGE,"E0.bottom"),sQuery(id+"F0.wireOp",EDGE,"E0.top"),sQuery(id+"F0.wireOp",EDGE,"E0.left"),sQuery(id+"F0.wireOp",EDGE,"E1")])],"isStart":true}),makeQuery(id+"F3.opExtrude","SWEPT_FACE",FACE,{"disambiguationData":[OSD([sQuery(id+"F2.wireOp",EDGE,"E13.right")])]})]});
            var Q67;
            Q67=makeQuery(id+"F3.boolean.opBoolean","INTERSECT",EDGE,{"derivedFrom":[makeQuery(id+"F1.opExtrude","CAP_FACE",FACE,{"disambiguationData":[OSD([sQuery(id+"F0.wireOp",EDGE,"E0.bottom"),sQuery(id+"F0.wireOp",EDGE,"E0.top"),sQuery(id+"F0.wireOp",EDGE,"E0.left"),sQuery(id+"F0.wireOp",EDGE,"E1")])],"isStart":true}),makeQuery(id+"F3.opExtrude","SWEPT_FACE",FACE,{"disambiguationData":[OSD([sQuery(id+"F2.wireOp",EDGE,"E14.left")])]})]});
            var Q68;
            Q68=makeQuery(id+"F3.boolean.opBoolean","INTERSECT",EDGE,{"derivedFrom":[makeQuery(id+"F1.opExtrude","CAP_FACE",FACE,{"disambiguationData":[OSD([sQuery(id+"F0.wireOp",EDGE,"E0.bottom"),sQuery(id+"F0.wireOp",EDGE,"E0.top"),sQuery(id+"F0.wireOp",EDGE,"E0.left"),sQuery(id+"F0.wireOp",EDGE,"E1")])],"isStart":true}),makeQuery(id+"F3.opExtrude","SWEPT_FACE",FACE,{"disambiguationData":[OSD([sQuery(id+"F2.wireOp",EDGE,"E14.top")])]})]});
            var Q69;
            Q69=makeQuery(id+"F3.boolean.opBoolean","INTERSECT",EDGE,{"derivedFrom":[makeQuery(id+"F1.opExtrude","CAP_FACE",FACE,{"disambiguationData":[OSD([sQuery(id+"F0.wireOp",EDGE,"E0.bottom"),sQuery(id+"F0.wireOp",EDGE,"E0.top"),sQuery(id+"F0.wireOp",EDGE,"E0.left"),sQuery(id+"F0.wireOp",EDGE,"E1")])],"isStart":true}),makeQuery(id+"F3.opExtrude","SWEPT_FACE",FACE,{"disambiguationData":[OSD([sQuery(id+"F2.wireOp",EDGE,"E14.right")])]})]});
            var Q70;
            Q70=makeQuery(id+"F3.boolean.opBoolean","INTERSECT",EDGE,{"derivedFrom":[makeQuery(id+"F1.opExtrude","CAP_FACE",FACE,{"disambiguationData":[OSD([sQuery(id+"F0.wireOp",EDGE,"E0.bottom"),sQuery(id+"F0.wireOp",EDGE,"E0.top"),sQuery(id+"F0.wireOp",EDGE,"E0.left"),sQuery(id+"F0.wireOp",EDGE,"E1")])],"isStart":true}),makeQuery(id+"F3.opExtrude","SWEPT_FACE",FACE,{"disambiguationData":[OSD([sQuery(id+"F2.wireOp",EDGE,"E15.left")])]})]});
            var Q71;
            Q71=makeQuery(id+"F3.boolean.opBoolean","INTERSECT",EDGE,{"derivedFrom":[makeQuery(id+"F1.opExtrude","CAP_FACE",FACE,{"disambiguationData":[OSD([sQuery(id+"F0.wireOp",EDGE,"E0.bottom"),sQuery(id+"F0.wireOp",EDGE,"E0.top"),sQuery(id+"F0.wireOp",EDGE,"E0.left"),sQuery(id+"F0.wireOp",EDGE,"E1")])],"isStart":true}),makeQuery(id+"F3.opExtrude","SWEPT_FACE",FACE,{"disambiguationData":[OSD([sQuery(id+"F2.wireOp",EDGE,"E15.top")])]})]});
            var Q72;
            Q72=makeQuery(id+"F3.boolean.opBoolean","INTERSECT",EDGE,{"derivedFrom":[makeQuery(id+"F1.opExtrude","CAP_FACE",FACE,{"disambiguationData":[OSD([sQuery(id+"F0.wireOp",EDGE,"E0.bottom"),sQuery(id+"F0.wireOp",EDGE,"E0.top"),sQuery(id+"F0.wireOp",EDGE,"E0.left"),sQuery(id+"F0.wireOp",EDGE,"E1")])],"isStart":true}),makeQuery(id+"F3.opExtrude","SWEPT_FACE",FACE,{"disambiguationData":[OSD([sQuery(id+"F2.wireOp",EDGE,"E15.right")])]})]});
            var Q73;
            Q73=makeQuery(id+"F3.boolean.opBoolean","INTERSECT",EDGE,{"derivedFrom":[makeQuery(id+"F1.opExtrude","CAP_FACE",FACE,{"disambiguationData":[OSD([sQuery(id+"F0.wireOp",EDGE,"E0.bottom"),sQuery(id+"F0.wireOp",EDGE,"E0.top"),sQuery(id+"F0.wireOp",EDGE,"E0.left"),sQuery(id+"F0.wireOp",EDGE,"E1")])],"isStart":true}),makeQuery(id+"F3.opExtrude","SWEPT_FACE",FACE,{"disambiguationData":[OSD([sQuery(id+"F2.wireOp",EDGE,"E16.left")])]})]});
            var Q74;
            Q74=makeQuery(id+"F3.boolean.opBoolean","INTERSECT",EDGE,{"derivedFrom":[makeQuery(id+"F1.opExtrude","CAP_FACE",FACE,{"disambiguationData":[OSD([sQuery(id+"F0.wireOp",EDGE,"E0.bottom"),sQuery(id+"F0.wireOp",EDGE,"E0.top"),sQuery(id+"F0.wireOp",EDGE,"E0.left"),sQuery(id+"F0.wireOp",EDGE,"E1")])],"isStart":true}),makeQuery(id+"F3.opExtrude","SWEPT_FACE",FACE,{"disambiguationData":[OSD([sQuery(id+"F2.wireOp",EDGE,"E16.top")])]})]});
            var Q75;
            Q75=makeQuery(id+"F3.boolean.opBoolean","INTERSECT",EDGE,{"derivedFrom":[makeQuery(id+"F1.opExtrude","CAP_FACE",FACE,{"disambiguationData":[OSD([sQuery(id+"F0.wireOp",EDGE,"E0.bottom"),sQuery(id+"F0.wireOp",EDGE,"E0.top"),sQuery(id+"F0.wireOp",EDGE,"E0.left"),sQuery(id+"F0.wireOp",EDGE,"E1")])],"isStart":true}),makeQuery(id+"F3.opExtrude","SWEPT_FACE",FACE,{"disambiguationData":[OSD([sQuery(id+"F2.wireOp",EDGE,"E16.right")])]})]});
            fillet(context, id + "F4", {"entities" : qUnion([Q0, Q1, Q2, Q3, Q4, Q5, Q6, Q7, Q8, Q9, Q10, Q11, Q12, Q13, Q14, Q15, Q16, Q17, Q18, Q19, Q20, Q21, Q22, Q23, Q24, Q25, Q26, Q27, Q28, Q29, Q30, Q31, Q32, Q33, Q34, Q35, Q36, Q37, Q38, Q39, Q40, Q41, Q42, Q43, Q44, Q45, Q46, Q47, Q48, Q49, Q50, Q51, Q52, Q53, Q54, Q55, Q56, Q57, Q58, Q59, Q60, Q61, Q62, Q63, Q64, Q65, Q66, Q67, Q68, Q69, Q70, Q71, Q72, Q73, Q74, Q75]), "radius" : 50.8 * mm, "tangentPropagation" : true, "allowEdgeOverflow" : false});
        }
        {
            var Q0;
            Q0=makeQuery(id+"F1.opExtrude","CAP_EDGE",EDGE,{"disambiguationData":[OSD([sQuery(id+"F0.wireOp",EDGE,"E0.bottom")])],"isStart":true});
            var Q1;
            Q1=makeQuery(id+"F1.opExtrude","CAP_EDGE",EDGE,{"disambiguationData":[OSD([sQuery(id+"F0.wireOp",EDGE,"E0.bottom")])],"isStart":false});
            chamfer(context, id + "F5", {"entities" : qUnion([Q0, Q1]), "width" : 25.4 * mm, "tangentPropagation" : true});
        }
    });
